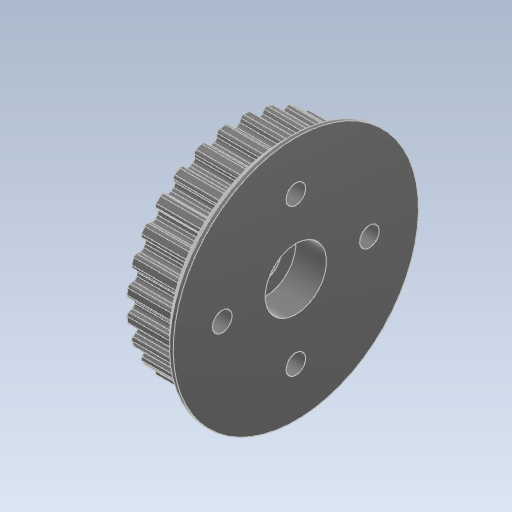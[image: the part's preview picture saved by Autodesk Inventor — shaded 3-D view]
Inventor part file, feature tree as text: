
AUTODESK INVENTOR PART (.ipt)
format: ipt  version: 2024 (Build 280153000, 153)  size: 571,392 bytes
history: native  units: mm
features: other x4, sketch x2, revolve x2, extrude x1, fillet x1
ambient origin geometry x8: Origin, YZ Plane, XZ Plane, XY Plane, X Axis, Y Axis, Z Axis, Center Point
bodies: Solid1 (feature_tree)
feature tree (10):
  other  "brideye_elbowUnit_pully-origin.ipt"
  sketch  "スケッチ3"
  extrude  "押し出し2"  Depth=10.0mm
  revolve  "回転6"
  revolve  "回転7"
  fillet  "フィレット2"  Radius=40.0mm
  other  "Solid1::brideye_elbowUnit_pully-origin.ipt"
  other  "TaggingFeature2"
  other  "スケッチ3_1"
  sketch  "スケッチ5"
